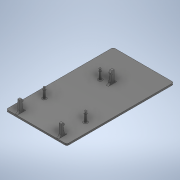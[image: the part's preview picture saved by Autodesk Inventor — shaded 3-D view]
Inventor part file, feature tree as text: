
AUTODESK INVENTOR PART (.ipt)
format: ipt  version: 2022 (Build 260153000, 153)  size: 219,648 bytes
history: native  units: mm
features: extrude x5, sketch x5, fillet x3, plane x2, mirror x1
ambient origin geometry x8: Origin, YZ Plane, XZ Plane, XY Plane, X Axis, Y Axis, Z Axis, Center Point
bodies: Solid1 (feature_tree)
feature tree (16):
  extrude  "Extrusion1"  Depth=127.0mm
  extrude  "Extrusion8"  Depth=3.0mm
  fillet  "Fillet3"  Radius=9.0mm
  extrude  "Extrusion9"  Depth=2.5mm
  fillet  "Fillet4"  Radius=2.5mm
  fillet  "Fillet5"  Radius=2.5mm
  plane  "Work Plane1"
  extrude  "Extrusion11"  Depth=0.5mm
  plane  "Work Plane2"
  mirror  "Mirror1"
  extrude  "Extrusion12"  Depth=0.5mm
  sketch  "Sketch1"  dims[d0=72.0mm d1=127.0mm]
  sketch  "Sketch2"  dims[d2=2.0mm d3=0.0mm d34=3.0mm d62=9.0mm d63=0.0mm]
  sketch  "Sketch8"  dims[d64=1.0mm d65=2.5mm d66=2.5mm d67=2.5mm]
  sketch  "Sketch10"  dims[d68=3.0mm d69=0.0mm d70=0.5mm]
  sketch  "Sketch11"  dims[d82=2.0mm d83=70.0mm d84=82.45mm d85=27.8mm d86=10.5mm d87=24.35mm d88=10.5mm d89=2.25mm d90=6.0mm d91=-11.5mm d92=10.0mm d96=1.0mm d98=3.0mm d100=2.5mm d102=1.5mm d103=3.0mm d105=2.5mm d106=0.0mm d107=10.0mm d109=2.5mm d112=3.0mm d113=3.0mm d115=2.5mm d116=0.0mm d117=10.9mm d118=1.0mm d119=1.5mm d120=10.9mm d121=0.5mm d122=82.45mm]
